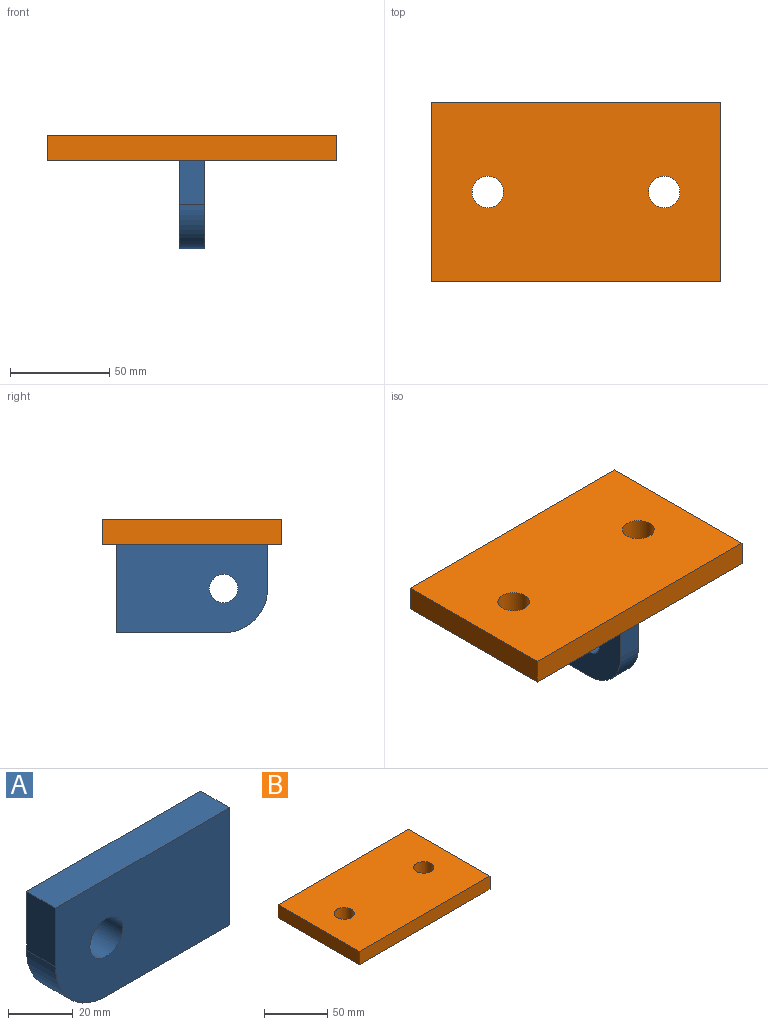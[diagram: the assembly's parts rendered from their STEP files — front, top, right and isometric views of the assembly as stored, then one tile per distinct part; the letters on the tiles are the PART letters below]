
ASSEMBLY  parts=2 mates=1
PART A: 8 faces, bbox 76.2x12.7x44.5 mm
  f0: plane 76.2x12.7mm, normal (0,0,1), area 967.7mm2, adj f1,f5,f6,f7
  f1: plane 22.23x12.7mm, normal (-1,0,0), area 282.3mm2, adj f0,f2,f6,f7
  f2: cylinder r=22.23mm len=22.23mm, axis (0,1,0), area 443.4mm2, adj f1,f3,f6,f7
  f3: plane 53.98x12.7mm, normal (0,0,-1), area 685.5mm2, adj f2,f5,f6,f7
  f4: cylinder r=7.14mm len=14.29mm, axis (0,1,0), area 570mm2, adj f6,f7
  f5: plane 44.45x12.7mm, normal (1,0,0), area 564.5mm2, adj f0,f3,f6,f7
  f6: plane 76.2x44.45mm, normal (0,-1,0), area 3120.8mm2, adj f0,f1,f2,f3,f4,f5
  f7: plane 76.2x44.45mm, normal (0,1,0), area 3120.8mm2, adj f0,f1,f2,f3,f4,f5
PART B: 8 faces, bbox 146.1x90.5x12.7 mm
  f0: plane 90.49x12.7mm, normal (-1,0,0), area 1149.2mm2, adj f1,f4,f6,f7
  f1: plane 146.05x12.7mm, normal (0,-1,0), area 1854.8mm2, adj f0,f2,f6,f7
  f2: plane 90.49x12.7mm, normal (1,0,0), area 1149.2mm2, adj f1,f4,f6,f7
  f3: cylinder r=7.94mm len=15.88mm, axis (0,0,-1), area 633.4mm2, adj f6,f7
  f4: plane 146.05x12.7mm, normal (0,1,0), area 1854.8mm2, adj f0,f2,f6,f7
  f5: cylinder r=7.94mm len=15.88mm, axis (0,0,-1), area 633.4mm2, adj f6,f7
  f6: plane 146.05x90.49mm, normal (0,0,1), area 12819.8mm2, adj f0,f1,f2,f3,f4,f5
  f7: plane 146.05x90.49mm, normal (0,0,-1), area 12819.8mm2, adj f0,f1,f2,f3,f4,f5
PLACE A rot(axis=(0,0,1),90deg) t=(0.61,-46.82,-58.5)mm
PLACE B t=(0.61,-30.94,-29.92)mm
MATE fastened B.f7 <-> A.f0  axis (0,0,-1) through (0.61,-30.94,-36.27)mm
